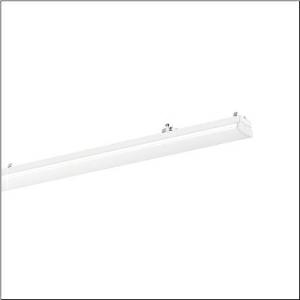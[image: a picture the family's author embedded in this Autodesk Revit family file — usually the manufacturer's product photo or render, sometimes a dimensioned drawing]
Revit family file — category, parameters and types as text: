
# Revit family: licross_11_recessed_opal_ho_51tl1dmn4d5m
name_source: partatom
category: Lighting Fixtures
units: mm (PartAtom-declared; Revit-internal decimal feet)

## family parameters
Cut with Voids When Loaded = No
Host = Face
Light Source = No
Part Type = Normal
Room Calculation Point = No
Round Connector Dimension = Use Diameter
Shared = No

## types (1)
- --- (1 x LED, 13690 lm, 74.5 W, 4000K)
    Apparent Load = 75 VA
    CIE Flux Codes = 44 73 91 87 100
    Color Rendering = 80
    Color Temperature = 4000K
    Default Elevation = 1800 mm
    Description = Licross 11 recessed opal HO, luminaire insert, of sheet steel, coil coated, white, length: 1.500mm, width: 76mm, height: 87mm, LED rated luminous flux: 13.690lm, light colour: 840, SDCM (Standard Deviation of Colour Matching)MacAdam ≤ 2 SDCM (initial), control gear: ON/OFF Multilumen, with plug, 3-pole, with phase selection, mains connection: 220..240V, AC, 50/60Hz, rated input power: 75W, internal wiring halogen-free, primary optical cover: cover, of PMMA, light emission: direct with ceiling illumination distribution, primary light characteristic: symmetric, protection rating (complete): IP40, insulation class (complete): insulation class I (protective earthing), certification: CE, ENEC, VDE, UKCA, protection symbol: D if used in an environment without relevant dust loads with corresponding accessories, impact resistance: IK06, permissible ambient temperature for indoor applications: -35..+35°C, corresponds to IFS (International Featured Standards) requirements for safety and quality in the food industry, reducing of maximum allowable ambient temperature of 5°C with ceiling mounting, The light source and the operating device comply with the requirements of the Ecodesign Regulation (EU) 2019/2020 and are replaceable in accordance with this regulation, packaging unit: 1 piece
    Height = 83 mm
    Lamp = 1 x LED
    Lamp Light Flux = 13690 lm
    Lamp Power = 74.5 W
    Lamp count = 1
    Length = 1500 mm
    Luminous efficacy = 184 lm/W
    Manufacturer = Siteco
    ModVariant = No
    Model = 51TL1DMN4D5M
    Mounting Place = Ceiling
    Mounting Type = Pendant
    Number of Poles = 1
    OnlyDefault = Yes
    Power Factor = 1
    Product Name = Licross 11 recessed opal HO
    Product group = luminaire insert | ceiling pendant
    ProductGroupID = 901
    Protection Class = Protection class I
    Protection Degree = IP 40
    RLX_Detail_Level = 1
    RLX_Emergency_Light_Flux = 0 lm
    RLX_Emergency_Type = 0
    RLX_Emergency_Type_DB = No
    RlxData = <blob elided: 24981 chars, md5=8a90531a>
    Socket = socket
    Standby Power = 0 W
    System Light Flux = 13690 lm
    System Power = 75 W
    Type Comments = factory setting: luminous flux: 100 % | (A | C | E) | 174 mA
    Type Image = l_1313666.jpg
    URL = http://relux.com
    VarID = @adj_083551
    Voltage = 0 V
    Weight = 0.00 kg
    Width = 76 mm

## geometry (parser evidence)
native form markers: Blend x4, Sweep x13
no freeform markers — native parametric forms only
